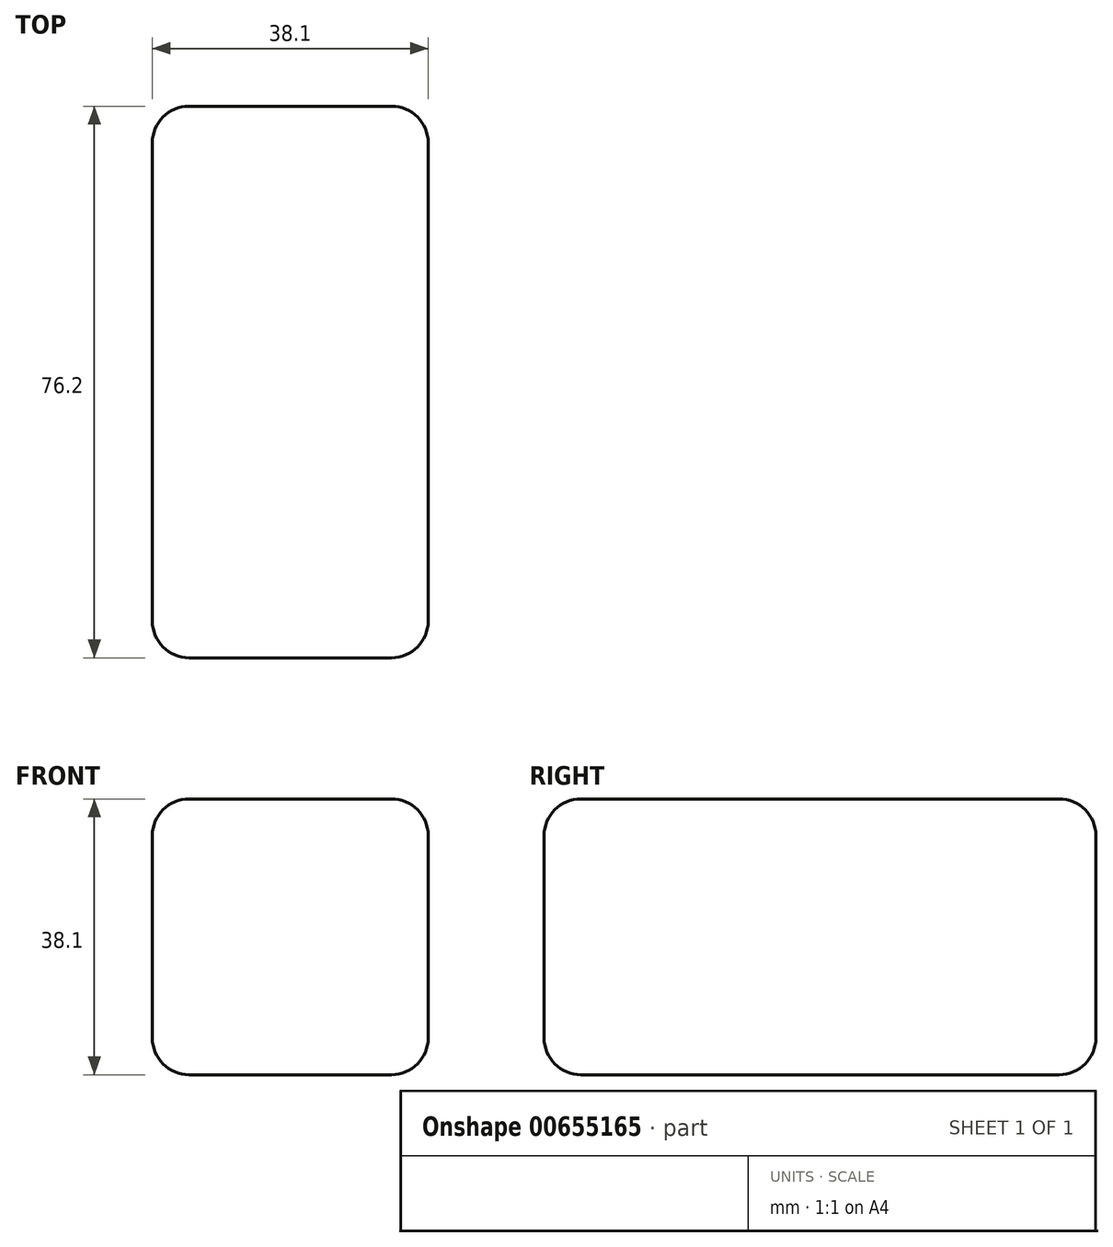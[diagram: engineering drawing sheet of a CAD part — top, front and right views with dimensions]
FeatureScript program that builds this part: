
annotation { "Feature Type Name" : "Feature", "Feature Type Description" : "" }
export const myFeature = defineFeature(function(context is Context, id is Id, definition is map)
    precondition{}
    {
        {
            var Q0;
            Q0=qCreatedBy(makeId("Top.planeOp"),FACE);
            var sketch = newSketch(context, id + "F0", { "sketchPlane" : qUnion([Q0])});
            skLineSegment(sketch, "E0.bottom", {"start": v(-19.05, 38.1) * mm, "end": v(19.05, 38.1) * mm});
            skLineSegment(sketch, "E0.top", {"start": v(-19.05, -38.1) * mm, "end": v(19.05, -38.1) * mm});
            skLineSegment(sketch, "E0.left", {"start": v(-19.05, 38.1) * mm, "end": v(-19.05, -38.1) * mm});
            skLineSegment(sketch, "E0.right", {"start": v(19.05, 38.1) * mm, "end": v(19.05, -38.1) * mm});
            skPoint(sketch, "E0.middle", {"position": v(0, 0) * mm});
            skSolve(sketch);
        }
        {
            var Q0;
            Q0=makeQuery(id+"F0.imprint","IMPRINT",FACE,{"disambiguationData":[TD([[makeQuery(id+"F0.imprint","IMPRINT",EDGE,{"derivedFrom":sQuery(id+"F0.wireOp",EDGE,"E0.bottom")}),-1.0]])]});
            extrude(context, id + "F1", {"entities" : qUnion([Q0]), "depth" : 38.1 * mm, "offsetDistance" : 25.4 * mm});
        }
        {
            var Q0;
            Q0=makeQuery(id+"F1.opExtrude","CAP_FACE",FACE,{"disambiguationData":[OSD([sQuery(id+"F0.wireOp",EDGE,"E0.bottom"),sQuery(id+"F0.wireOp",EDGE,"E0.top"),sQuery(id+"F0.wireOp",EDGE,"E0.left"),sQuery(id+"F0.wireOp",EDGE,"E0.right")])],"isStart":true});
            var Q1;
            Q1=makeQuery(id+"F1.opExtrude","SWEPT_FACE",FACE,{"disambiguationData":[OSD([sQuery(id+"F0.wireOp",EDGE,"E0.top")])]});
            var Q2;
            Q2=makeQuery(id+"F1.opExtrude","SWEPT_FACE",FACE,{"disambiguationData":[OSD([sQuery(id+"F0.wireOp",EDGE,"E0.right")])]});
            var Q3;
            Q3=makeQuery(id+"F1.opExtrude","SWEPT_FACE",FACE,{"disambiguationData":[OSD([sQuery(id+"F0.wireOp",EDGE,"E0.bottom")])]});
            var Q4;
            Q4=makeQuery(id+"F1.opExtrude","SWEPT_FACE",FACE,{"disambiguationData":[OSD([sQuery(id+"F0.wireOp",EDGE,"E0.left")])]});
            fillet(context, id + "F2", {"entities" : qUnion([Q0, Q1, Q2, Q3, Q4]), "radius" : 5.08 * mm, "tangentPropagation" : true, "allowEdgeOverflow" : false});
        }
    });
